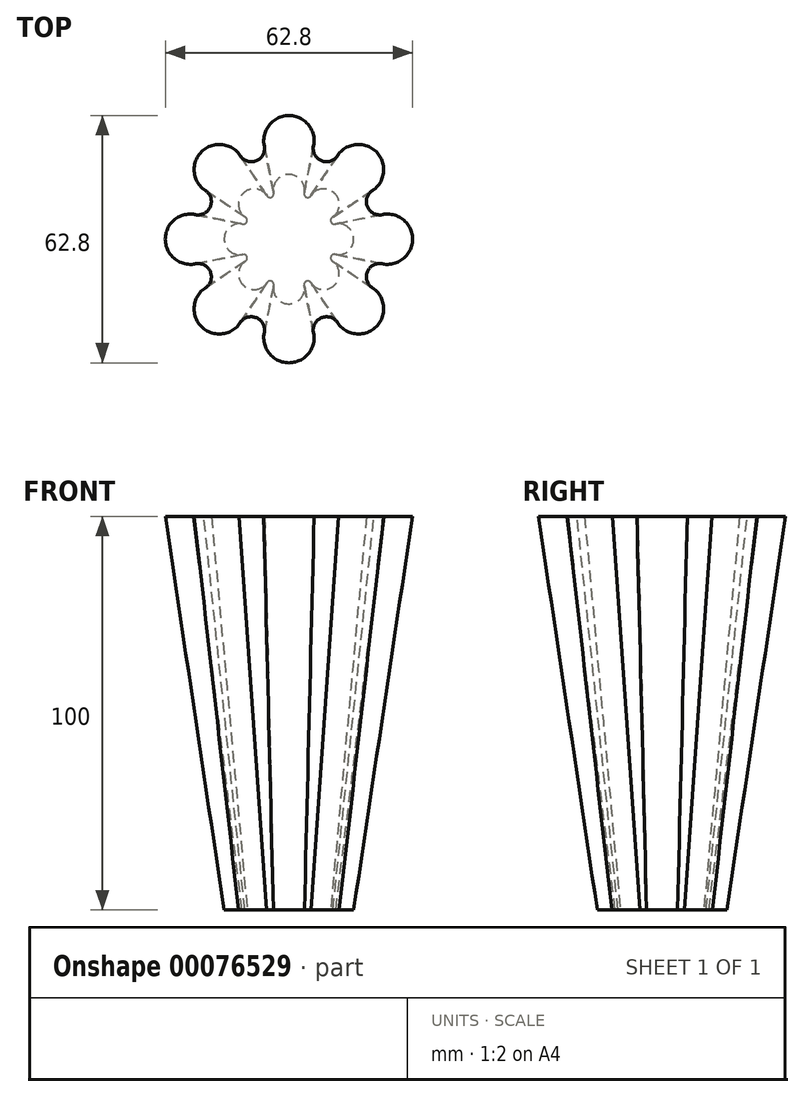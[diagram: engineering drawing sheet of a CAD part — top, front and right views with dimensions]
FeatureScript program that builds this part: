
annotation { "Feature Type Name" : "Feature", "Feature Type Description" : "" }
export const myFeature = defineFeature(function(context is Context, id is Id, definition is map)
    precondition{}
    {
        {
            var Q0;
            Q0=qCreatedBy(makeId("Top.planeOp"),FACE);
            var sketch = newSketch(context, id + "F0", { "sketchPlane" : qUnion([Q0])});
            skCircle(sketch, "E0", {"center": v(0, 0) * mm, "radius": 12.5 * mm, "construction": true});
            skArc(sketch, "E1", {"start": v(2.44, 12.26) * mm, "mid": v(0, 14.95) * mm, "end": v(-2.44, 12.26) * mm, "construction": true});
            skLineSegment(sketch, "E2", {"start": v(-2.44, 12.26) * mm, "end": v(0, 0) * mm, "construction": true});
            skLineSegment(sketch, "E3", {"start": v(2.44, 12.26) * mm, "end": v(0, 0) * mm, "construction": true});
            skArc(sketch, "E4.1.0", {"start": v(-6.94, 10.4) * mm, "mid": v(-10.57, 10.57) * mm, "end": v(-10.4, 6.94) * mm, "construction": true});
            skArc(sketch, "E4.2.0", {"start": v(-12.26, 2.44) * mm, "mid": v(-14.95, 0) * mm, "end": v(-12.26, -2.44) * mm, "construction": true});
            skArc(sketch, "E4.3.0", {"start": v(-10.4, -6.94) * mm, "mid": v(-10.57, -10.57) * mm, "end": v(-6.94, -10.4) * mm, "construction": true});
            skArc(sketch, "E4.4.0", {"start": v(-2.44, -12.26) * mm, "mid": v(0, -14.95) * mm, "end": v(2.44, -12.26) * mm, "construction": true});
            skArc(sketch, "E4.5.0", {"start": v(6.94, -10.4) * mm, "mid": v(10.57, -10.57) * mm, "end": v(10.4, -6.94) * mm, "construction": true});
            skArc(sketch, "E4.6.0", {"start": v(12.26, -2.44) * mm, "mid": v(14.95, 0) * mm, "end": v(12.26, 2.44) * mm, "construction": true});
            skArc(sketch, "E4.7.0", {"start": v(10.4, 6.94) * mm, "mid": v(10.57, 10.57) * mm, "end": v(6.94, 10.4) * mm, "construction": true});
            skArc(sketch, "E5", {"start": v(2.44, 12.26) * mm, "mid": v(3.85, 9.28) * mm, "end": v(6.94, 10.4) * mm, "construction": true});
            skArc(sketch, "E6.1.0", {"start": v(-6.94, 10.4) * mm, "mid": v(-3.85, 9.28) * mm, "end": v(-2.44, 12.26) * mm, "construction": true});
            skArc(sketch, "E6.2.0", {"start": v(-12.26, 2.44) * mm, "mid": v(-9.28, 3.85) * mm, "end": v(-10.4, 6.94) * mm, "construction": true});
            skArc(sketch, "E6.3.0", {"start": v(-10.4, -6.94) * mm, "mid": v(-9.28, -3.85) * mm, "end": v(-12.26, -2.44) * mm, "construction": true});
            skArc(sketch, "E6.4.0", {"start": v(-2.44, -12.26) * mm, "mid": v(-3.85, -9.28) * mm, "end": v(-6.94, -10.4) * mm, "construction": true});
            skArc(sketch, "E6.5.0", {"start": v(6.94, -10.4) * mm, "mid": v(3.85, -9.28) * mm, "end": v(2.44, -12.26) * mm, "construction": true});
            skArc(sketch, "E6.6.0", {"start": v(12.26, -2.44) * mm, "mid": v(9.28, -3.85) * mm, "end": v(10.4, -6.94) * mm, "construction": true});
            skArc(sketch, "E6.7.0", {"start": v(10.4, 6.94) * mm, "mid": v(9.28, 3.85) * mm, "end": v(12.26, 2.44) * mm, "construction": true});
            skArc(sketch, "E7.0", {"start": v(11.19, 5.66) * mm, "mid": v(11.63, 11.63) * mm, "end": v(5.66, 11.19) * mm});
            skArc(sketch, "E7.1", {"start": v(3.9, 11.92) * mm, "mid": v(4.42, 10.67) * mm, "end": v(5.66, 11.19) * mm});
            skArc(sketch, "E7.2", {"start": v(3.9, 11.92) * mm, "mid": v(0, 16.45) * mm, "end": v(-3.9, 11.92) * mm});
            skArc(sketch, "E7.3", {"start": v(-5.66, 11.19) * mm, "mid": v(-4.42, 10.67) * mm, "end": v(-3.9, 11.92) * mm});
            skArc(sketch, "E7.4", {"start": v(-5.66, 11.19) * mm, "mid": v(-11.63, 11.63) * mm, "end": v(-11.19, 5.66) * mm});
            skArc(sketch, "E7.5", {"start": v(5.66, -11.19) * mm, "mid": v(4.42, -10.67) * mm, "end": v(3.9, -11.92) * mm});
            skArc(sketch, "E7.6", {"start": v(5.66, -11.19) * mm, "mid": v(11.63, -11.63) * mm, "end": v(11.19, -5.66) * mm});
            skArc(sketch, "E7.7", {"start": v(11.92, -3.9) * mm, "mid": v(10.67, -4.42) * mm, "end": v(11.19, -5.66) * mm});
            skArc(sketch, "E7.8", {"start": v(11.92, -3.9) * mm, "mid": v(16.45, 0) * mm, "end": v(11.92, 3.9) * mm});
            skArc(sketch, "E7.9", {"start": v(-3.9, -11.92) * mm, "mid": v(0, -16.45) * mm, "end": v(3.9, -11.92) * mm});
            skArc(sketch, "E7.10", {"start": v(-3.9, -11.92) * mm, "mid": v(-4.42, -10.67) * mm, "end": v(-5.66, -11.19) * mm});
            skArc(sketch, "E7.11", {"start": v(-11.19, -5.66) * mm, "mid": v(-11.63, -11.63) * mm, "end": v(-5.66, -11.19) * mm});
            skArc(sketch, "E7.12", {"start": v(-11.19, -5.66) * mm, "mid": v(-10.67, -4.42) * mm, "end": v(-11.92, -3.9) * mm});
            skArc(sketch, "E7.13", {"start": v(-11.92, 3.9) * mm, "mid": v(-16.45, 0) * mm, "end": v(-11.92, -3.9) * mm});
            skArc(sketch, "E7.14", {"start": v(11.19, 5.66) * mm, "mid": v(10.67, 4.42) * mm, "end": v(11.92, 3.9) * mm});
            skArc(sketch, "E7.15", {"start": v(-11.92, 3.9) * mm, "mid": v(-10.67, 4.42) * mm, "end": v(-11.19, 5.66) * mm});
            skArc(sketch, "E8.0", {"start": v(-8.17, 9.51) * mm, "mid": v(-3.27, 7.9) * mm, "end": v(-0.95, 12.5) * mm, "construction": true});
            skArc(sketch, "E8.1", {"start": v(0.95, 12.5) * mm, "mid": v(0, 13.45) * mm, "end": v(-0.95, 12.5) * mm, "construction": true});
            skArc(sketch, "E8.2", {"start": v(0.95, 12.5) * mm, "mid": v(3.27, 7.9) * mm, "end": v(8.17, 9.51) * mm, "construction": true});
            skArc(sketch, "E8.3", {"start": v(9.51, 8.17) * mm, "mid": v(9.51, 9.51) * mm, "end": v(8.17, 9.51) * mm, "construction": true});
            skArc(sketch, "E8.4", {"start": v(9.51, 8.17) * mm, "mid": v(7.9, 3.27) * mm, "end": v(12.5, 0.95) * mm, "construction": true});
            skArc(sketch, "E8.5", {"start": v(-9.51, -8.17) * mm, "mid": v(-9.51, -9.51) * mm, "end": v(-8.17, -9.51) * mm, "construction": true});
            skArc(sketch, "E8.6", {"start": v(-9.51, -8.17) * mm, "mid": v(-7.9, -3.27) * mm, "end": v(-12.5, -0.95) * mm, "construction": true});
            skArc(sketch, "E8.7", {"start": v(-12.5, 0.95) * mm, "mid": v(-13.45, 0) * mm, "end": v(-12.5, -0.95) * mm, "construction": true});
            skArc(sketch, "E8.8", {"start": v(-12.5, 0.95) * mm, "mid": v(-7.9, 3.27) * mm, "end": v(-9.51, 8.17) * mm, "construction": true});
            skArc(sketch, "E8.9", {"start": v(-0.95, -12.5) * mm, "mid": v(-3.27, -7.9) * mm, "end": v(-8.17, -9.51) * mm, "construction": true});
            skArc(sketch, "E8.10", {"start": v(-0.95, -12.5) * mm, "mid": v(0, -13.45) * mm, "end": v(0.95, -12.5) * mm, "construction": true});
            skArc(sketch, "E8.11", {"start": v(8.17, -9.51) * mm, "mid": v(3.27, -7.9) * mm, "end": v(0.95, -12.5) * mm, "construction": true});
            skArc(sketch, "E8.12", {"start": v(8.17, -9.51) * mm, "mid": v(9.51, -9.51) * mm, "end": v(9.51, -8.17) * mm, "construction": true});
            skArc(sketch, "E8.13", {"start": v(12.5, -0.95) * mm, "mid": v(7.9, -3.27) * mm, "end": v(9.51, -8.17) * mm, "construction": true});
            skArc(sketch, "E8.14", {"start": v(-8.17, 9.51) * mm, "mid": v(-9.51, 9.51) * mm, "end": v(-9.51, 8.17) * mm, "construction": true});
            skArc(sketch, "E8.15", {"start": v(12.5, -0.95) * mm, "mid": v(13.45, 0) * mm, "end": v(12.5, 0.95) * mm, "construction": true});
            skSolve(sketch);
        }
        {
            var Q0;
            Q0=qCreatedBy(makeId("Top.planeOp"),FACE);
            cPlane(context, id + "F1", {"entities" : qUnion([Q0]), "cplaneType" : CPlaneType.OFFSET, "offset" : 100 * mm, "width" : 150 * mm, "height" : 150 * mm});
        }
        {
            var Q0;
            Q0=qCreatedBy(id+"F1.planeOp",FACE);
            var sketch = newSketch(context, id + "F2", { "sketchPlane" : qUnion([Q0])});
            skCircle(sketch, "E9", {"center": v(0, 0) * mm, "radius": 25 * mm, "construction": true});
            skArc(sketch, "E10", {"start": v(4.88, 24.52) * mm, "mid": v(0, 29.9) * mm, "end": v(-4.88, 24.52) * mm, "construction": true});
            skLineSegment(sketch, "E11", {"start": v(-4.88, 24.52) * mm, "end": v(0, 0) * mm, "construction": true});
            skLineSegment(sketch, "E12", {"start": v(4.88, 24.52) * mm, "end": v(0, 0) * mm, "construction": true});
            skArc(sketch, "E13.1.0", {"start": v(-13.89, 20.79) * mm, "mid": v(-21.14, 21.14) * mm, "end": v(-20.79, 13.89) * mm, "construction": true});
            skArc(sketch, "E13.2.0", {"start": v(-24.52, 4.88) * mm, "mid": v(-29.9, 0) * mm, "end": v(-24.52, -4.88) * mm, "construction": true});
            skArc(sketch, "E13.3.0", {"start": v(-20.79, -13.89) * mm, "mid": v(-21.14, -21.14) * mm, "end": v(-13.89, -20.79) * mm, "construction": true});
            skArc(sketch, "E13.4.0", {"start": v(-4.88, -24.52) * mm, "mid": v(0, -29.9) * mm, "end": v(4.88, -24.52) * mm, "construction": true});
            skArc(sketch, "E13.5.0", {"start": v(13.89, -20.79) * mm, "mid": v(21.14, -21.14) * mm, "end": v(20.79, -13.89) * mm, "construction": true});
            skArc(sketch, "E13.6.0", {"start": v(24.52, -4.88) * mm, "mid": v(29.9, 0) * mm, "end": v(24.52, 4.88) * mm, "construction": true});
            skArc(sketch, "E13.7.0", {"start": v(20.79, 13.89) * mm, "mid": v(21.14, 21.14) * mm, "end": v(13.89, 20.79) * mm, "construction": true});
            skArc(sketch, "E14", {"start": v(4.88, 24.52) * mm, "mid": v(7.7, 18.57) * mm, "end": v(13.89, 20.79) * mm, "construction": true});
            skArc(sketch, "E15.1.0", {"start": v(-13.89, 20.79) * mm, "mid": v(-7.7, 18.57) * mm, "end": v(-4.88, 24.52) * mm, "construction": true});
            skArc(sketch, "E15.2.0", {"start": v(-24.52, 4.88) * mm, "mid": v(-18.57, 7.7) * mm, "end": v(-20.79, 13.89) * mm, "construction": true});
            skArc(sketch, "E15.3.0", {"start": v(-20.79, -13.89) * mm, "mid": v(-18.57, -7.7) * mm, "end": v(-24.52, -4.88) * mm, "construction": true});
            skArc(sketch, "E15.4.0", {"start": v(-4.88, -24.52) * mm, "mid": v(-7.7, -18.57) * mm, "end": v(-13.89, -20.79) * mm, "construction": true});
            skArc(sketch, "E15.5.0", {"start": v(13.89, -20.79) * mm, "mid": v(7.7, -18.57) * mm, "end": v(4.88, -24.52) * mm, "construction": true});
            skArc(sketch, "E15.6.0", {"start": v(24.52, -4.88) * mm, "mid": v(18.57, -7.7) * mm, "end": v(20.79, -13.89) * mm, "construction": true});
            skArc(sketch, "E15.7.0", {"start": v(20.79, 13.89) * mm, "mid": v(18.57, 7.7) * mm, "end": v(24.52, 4.88) * mm, "construction": true});
            skArc(sketch, "E16.0", {"start": v(21.6, 12.62) * mm, "mid": v(22.2, 22.2) * mm, "end": v(12.62, 21.6) * mm});
            skArc(sketch, "E16.1", {"start": v(6.35, 24.2) * mm, "mid": v(8.27, 19.96) * mm, "end": v(12.62, 21.6) * mm});
            skArc(sketch, "E16.2", {"start": v(6.35, 24.2) * mm, "mid": v(0, 31.4) * mm, "end": v(-6.35, 24.2) * mm});
            skArc(sketch, "E16.3", {"start": v(-12.62, 21.6) * mm, "mid": v(-8.27, 19.96) * mm, "end": v(-6.35, 24.2) * mm});
            skArc(sketch, "E16.4", {"start": v(-12.62, 21.6) * mm, "mid": v(-22.2, 22.2) * mm, "end": v(-21.6, 12.62) * mm});
            skArc(sketch, "E16.5", {"start": v(12.62, -21.6) * mm, "mid": v(8.27, -19.96) * mm, "end": v(6.35, -24.2) * mm});
            skArc(sketch, "E16.6", {"start": v(12.62, -21.6) * mm, "mid": v(22.2, -22.2) * mm, "end": v(21.6, -12.62) * mm});
            skArc(sketch, "E16.7", {"start": v(24.2, -6.35) * mm, "mid": v(19.96, -8.27) * mm, "end": v(21.6, -12.62) * mm});
            skArc(sketch, "E16.8", {"start": v(24.2, -6.35) * mm, "mid": v(31.4, 0) * mm, "end": v(24.2, 6.35) * mm});
            skArc(sketch, "E16.9", {"start": v(-6.35, -24.2) * mm, "mid": v(0, -31.4) * mm, "end": v(6.35, -24.2) * mm});
            skArc(sketch, "E16.10", {"start": v(-6.35, -24.2) * mm, "mid": v(-8.27, -19.96) * mm, "end": v(-12.62, -21.6) * mm});
            skArc(sketch, "E16.11", {"start": v(-21.6, -12.62) * mm, "mid": v(-22.2, -22.2) * mm, "end": v(-12.62, -21.6) * mm});
            skArc(sketch, "E16.12", {"start": v(-21.6, -12.62) * mm, "mid": v(-19.96, -8.27) * mm, "end": v(-24.2, -6.35) * mm});
            skArc(sketch, "E16.13", {"start": v(-24.2, 6.35) * mm, "mid": v(-31.4, 0) * mm, "end": v(-24.2, -6.35) * mm});
            skArc(sketch, "E16.14", {"start": v(21.6, 12.62) * mm, "mid": v(19.96, 8.27) * mm, "end": v(24.2, 6.35) * mm});
            skArc(sketch, "E16.15", {"start": v(-24.2, 6.35) * mm, "mid": v(-19.96, 8.27) * mm, "end": v(-21.6, 12.62) * mm});
            skArc(sketch, "E17.0", {"start": v(-15.13, 19.93) * mm, "mid": v(-7.12, 17.18) * mm, "end": v(-3.4, 24.8) * mm, "construction": true});
            skArc(sketch, "E17.1", {"start": v(3.4, 24.8) * mm, "mid": v(0, 28.4) * mm, "end": v(-3.4, 24.8) * mm, "construction": true});
            skArc(sketch, "E17.2", {"start": v(3.4, 24.8) * mm, "mid": v(7.12, 17.18) * mm, "end": v(15.13, 19.93) * mm, "construction": true});
            skArc(sketch, "E17.3", {"start": v(19.93, 15.13) * mm, "mid": v(20.08, 20.08) * mm, "end": v(15.13, 19.93) * mm, "construction": true});
            skArc(sketch, "E17.4", {"start": v(19.93, 15.13) * mm, "mid": v(17.18, 7.12) * mm, "end": v(24.8, 3.4) * mm, "construction": true});
            skArc(sketch, "E17.5", {"start": v(-19.93, -15.13) * mm, "mid": v(-20.08, -20.08) * mm, "end": v(-15.13, -19.93) * mm, "construction": true});
            skArc(sketch, "E17.6", {"start": v(-19.93, -15.13) * mm, "mid": v(-17.18, -7.12) * mm, "end": v(-24.8, -3.4) * mm, "construction": true});
            skArc(sketch, "E17.7", {"start": v(-24.8, 3.4) * mm, "mid": v(-28.4, 0) * mm, "end": v(-24.8, -3.4) * mm, "construction": true});
            skArc(sketch, "E17.8", {"start": v(-24.8, 3.4) * mm, "mid": v(-17.18, 7.12) * mm, "end": v(-19.93, 15.13) * mm, "construction": true});
            skArc(sketch, "E17.9", {"start": v(-3.4, -24.8) * mm, "mid": v(-7.12, -17.18) * mm, "end": v(-15.13, -19.93) * mm, "construction": true});
            skArc(sketch, "E17.10", {"start": v(-3.4, -24.8) * mm, "mid": v(0, -28.4) * mm, "end": v(3.4, -24.8) * mm, "construction": true});
            skArc(sketch, "E17.11", {"start": v(15.13, -19.93) * mm, "mid": v(7.12, -17.18) * mm, "end": v(3.4, -24.8) * mm, "construction": true});
            skArc(sketch, "E17.12", {"start": v(15.13, -19.93) * mm, "mid": v(20.08, -20.08) * mm, "end": v(19.93, -15.13) * mm, "construction": true});
            skArc(sketch, "E17.13", {"start": v(24.8, -3.4) * mm, "mid": v(17.18, -7.12) * mm, "end": v(19.93, -15.13) * mm, "construction": true});
            skArc(sketch, "E17.14", {"start": v(-15.13, 19.93) * mm, "mid": v(-20.08, 20.08) * mm, "end": v(-19.93, 15.13) * mm, "construction": true});
            skArc(sketch, "E17.15", {"start": v(24.8, -3.4) * mm, "mid": v(28.4, 0) * mm, "end": v(24.8, 3.4) * mm, "construction": true});
            skPoint(sketch, "E18.0", {"position": v(11.55, 4.78) * mm});
            skSolve(sketch);
        }
        {
            var Q0;
            Q0 = qSketchRegion(id + "F0", true);
            var Q1;
            Q1 = qSketchRegion(id + "F2", true);
            loft(context, id + "F3", {"sheetProfilesArray" : [{ "sheetProfileEntities" : qUnion([Q0]) }, { "sheetProfileEntities" : qUnion([Q1]) }]});
        }
    });
